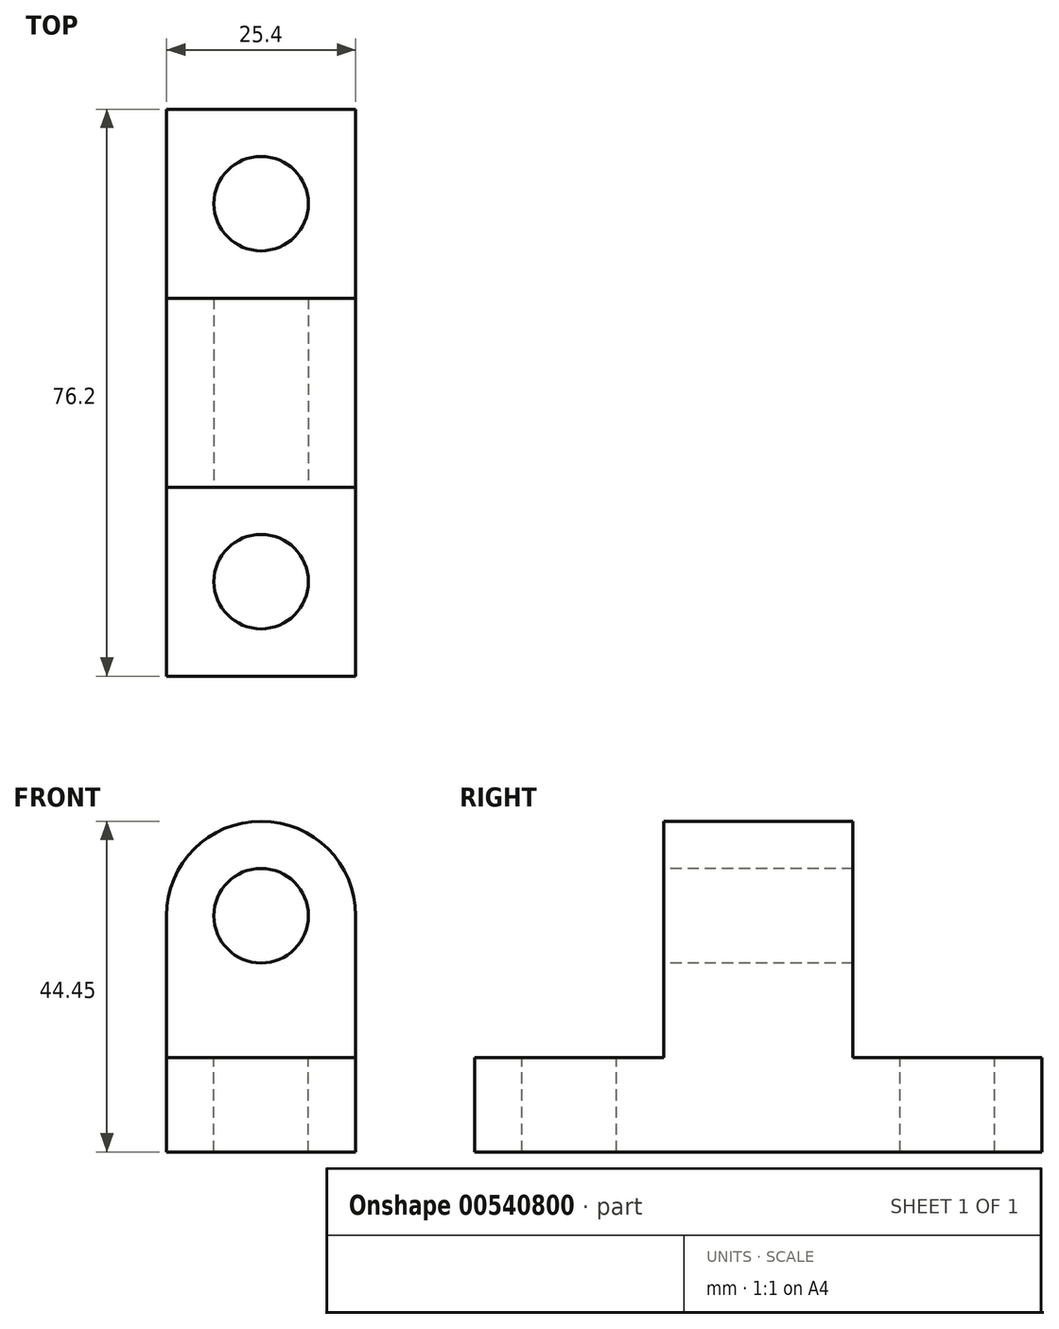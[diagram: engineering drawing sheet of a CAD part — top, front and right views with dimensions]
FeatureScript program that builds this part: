
annotation { "Feature Type Name" : "Feature", "Feature Type Description" : "" }
export const myFeature = defineFeature(function(context is Context, id is Id, definition is map)
    precondition{}
    {
        {
            var Q0;
            Q0=qCreatedBy(makeId("Top.planeOp"),FACE);
            var sketch = newSketch(context, id + "F0", { "sketchPlane" : qUnion([Q0])});
            skLineSegment(sketch, "E0", {"start": v(0, 0) * mm, "end": v(0, 76.2) * mm});
            skLineSegment(sketch, "E1", {"start": v(0, 76.2) * mm, "end": v(25.4, 76.2) * mm});
            skLineSegment(sketch, "E2", {"start": v(25.4, 76.2) * mm, "end": v(25.4, 0) * mm});
            skLineSegment(sketch, "E3", {"start": v(25.4, 0) * mm, "end": v(0, 0) * mm});
            skSolve(sketch);
        }
        {
            var Q0;
            Q0=makeQuery(id+"F0.imprint","IMPRINT",FACE,{"disambiguationData":[TD([[makeQuery(id+"F0.imprint","IMPRINT",EDGE,{"derivedFrom":sQuery(id+"F0.wireOp",EDGE,"E0")}),-1.0]])]});
            extrude(context, id + "F1", {"entities" : qUnion([Q0]), "depth" : 44.45 * mm, "offsetDistance" : 25.4 * mm});
        }
        {
            var Q0;
            Q0=makeQuery(id+"F1.opExtrude","SWEPT_FACE",FACE,{"disambiguationData":[OSD([sQuery(id+"F0.wireOp",EDGE,"E0")])]});
            var sketch = newSketch(context, id + "F2", { "sketchPlane" : qUnion([Q0])});
            skLineSegment(sketch, "E4", {"start": v(0, 12.7) * mm, "end": v(-25.4, 12.7) * mm});
            skLineSegment(sketch, "E5", {"start": v(-25.4, 12.7) * mm, "end": v(-25.4, 44.45) * mm});
            skLineSegment(sketch, "E6", {"start": v(-25.4, 44.45) * mm, "end": v(0, 44.45) * mm});
            skLineSegment(sketch, "E7", {"start": v(0, 44.45) * mm, "end": v(0, 12.7) * mm});
            skLineSegment(sketch, "E8", {"start": v(-76.2, 12.7) * mm, "end": v(-50.8, 12.7) * mm});
            skLineSegment(sketch, "E9", {"start": v(-50.8, 12.7) * mm, "end": v(-50.8, 44.45) * mm});
            skLineSegment(sketch, "E10", {"start": v(-50.8, 44.45) * mm, "end": v(-76.2, 44.45) * mm});
            skLineSegment(sketch, "E11", {"start": v(-76.2, 44.45) * mm, "end": v(-76.2, 12.7) * mm});
            skSolve(sketch);
        }
        {
            var Q0;
            Q0=makeQuery(id+"F2.imprint","IMPRINT",FACE,{"disambiguationData":[TD([[makeQuery(id+"F2.imprint","IMPRINT",EDGE,{"derivedFrom":sQuery(id+"F2.wireOp",EDGE,"E8")}),1.0]])]});
            var Q1;
            Q1=makeQuery(id+"F2.imprint","IMPRINT",FACE,{"disambiguationData":[TD([[makeQuery(id+"F2.imprint","IMPRINT",EDGE,{"derivedFrom":sQuery(id+"F2.wireOp",EDGE,"E4")}),-1.0]])]});
            extrude(context, id + "F3", {"entities" : qUnion([Q0, Q1]), "operationType" : NewBodyOperationType.REMOVE, "oppositeDirection" : true, "depth" : 25.4 * mm, "offsetDistance" : 25.4 * mm});
        }
        {
            var Q0;
            Q0=makeQuery(id+"F3.boolean.opBoolean","COPY",FACE,{"derivedFrom":makeQuery(id+"F3.opExtrude","SWEPT_FACE",FACE,{"disambiguationData":[OSD([sQuery(id+"F2.wireOp",EDGE,"E5")])]})});
            var sketch = newSketch(context, id + "F4", { "sketchPlane" : qUnion([Q0])});
            skLineSegment(sketch, "E12", {"start": v(25.4, 24.96) * mm, "end": v(25.4, 44.45) * mm});
            skLineSegment(sketch, "E13", {"start": v(25.4, 44.45) * mm, "end": v(0, 44.45) * mm});
            skLineSegment(sketch, "E14", {"start": v(0, 44.45) * mm, "end": v(0, 28.57) * mm});
            skArc(sketch, "E15", {"start": v(25.4, 31.75) * mm, "mid": v(12.7, 44.45) * mm, "end": v(0, 31.75) * mm});
            skSolve(sketch);
        }
        {
            var Q0;
            {var subQ0=sQuery(id+"F4.wireOp",EDGE,"E14");var subQ1=sQuery(id+"F4.wireOp",EDGE,"E13");var subQ2=makeQuery(id+"F4.imprint","INTERSECT",VERTEX,{"derivedFrom":[subQ1,subQ0]});Q0=makeQuery(id+"F4.imprint","IMPRINT",FACE,{"disambiguationData":[TD([[makeQuery(id+"F4.imprint","IMPRINT",EDGE,{"disambiguationData":[TD([[subQ2,1.0]])],"derivedFrom":subQ1}),1.0]])]});}
            var Q1;
            {var subQ0=sQuery(id+"F4.wireOp",EDGE,"E13");var subQ1=sQuery(id+"F4.wireOp",EDGE,"E12");var subQ2=makeQuery(id+"F4.imprint","INTERSECT",VERTEX,{"derivedFrom":[subQ1,subQ0]});Q1=makeQuery(id+"F4.imprint","IMPRINT",FACE,{"disambiguationData":[TD([[makeQuery(id+"F4.imprint","IMPRINT",EDGE,{"disambiguationData":[TD([[subQ2,1.0]])],"derivedFrom":subQ1}),1.0]])]});}
            extrude(context, id + "F5", {"entities" : qUnion([Q0, Q1]), "operationType" : NewBodyOperationType.REMOVE, "oppositeDirection" : true, "depth" : 25.4 * mm, "offsetDistance" : 25.4 * mm});
        }
        {
            var Q0;
            Q0=makeQuery(id+"F3.boolean.opBoolean","COPY",FACE,{"derivedFrom":makeQuery(id+"F3.opExtrude","SWEPT_FACE",FACE,{"disambiguationData":[OSD([sQuery(id+"F2.wireOp",EDGE,"E5")])]})});
            var sketch = newSketch(context, id + "F6", { "sketchPlane" : qUnion([Q0])});
            skLineSegment(sketch, "E16", {"start": v(25.4, 12.7) * mm, "end": v(25.4, 31.75) * mm});
            skLineSegment(sketch, "E17", {"start": v(0, 31.75) * mm, "end": v(0, 12.7) * mm});
            skLineSegment(sketch, "E18", {"start": v(0, 12.7) * mm, "end": v(25.4, 12.7) * mm});
            skEllipse(sketch, "E19", {"center": v(12.7, 31.75) * mm, "majorRadius": 6.35 * mm, "minorRadius": 6.35 * mm, "majorAxis": v(1, 0)});
            skSolve(sketch);
        }
        {
            var Q0;
            Q0=makeQuery(id+"F6.imprint","IMPRINT",FACE,{"disambiguationData":[TD([[makeQuery(id+"F6.imprint","IMPRINT",EDGE,{"derivedFrom":sQuery(id+"F6.wireOp",EDGE,"E19")}),1.0]])]});
            extrude(context, id + "F7", {"entities" : qUnion([Q0]), "operationType" : NewBodyOperationType.REMOVE, "oppositeDirection" : true, "depth" : 25.4 * mm, "offsetDistance" : 25.4 * mm});
        }
        {
            var Q0;
            Q0=makeQuery(id+"F3.boolean.opBoolean","COPY",FACE,{"derivedFrom":makeQuery(id+"F3.opExtrude","SWEPT_FACE",FACE,{"disambiguationData":[OSD([sQuery(id+"F2.wireOp",EDGE,"E4")])]})});
            var sketch = newSketch(context, id + "F8", { "sketchPlane" : qUnion([Q0])});
            skCircle(sketch, "E20", {"center": v(12.7, 12.7) * mm, "radius": 6.35 * mm});
            skSolve(sketch);
        }
        {
            var Q0;
            Q0 = qSketchRegion(id + "F8", true);
            extrude(context, id + "F9", {"entities" : qUnion([Q0]), "operationType" : NewBodyOperationType.REMOVE, "oppositeDirection" : true, "depth" : 25.4 * mm, "offsetDistance" : 25.4 * mm});
        }
        {
            var Q0;
            Q0=makeQuery(id+"F3.boolean.opBoolean","COPY",FACE,{"derivedFrom":makeQuery(id+"F3.opExtrude","SWEPT_FACE",FACE,{"disambiguationData":[OSD([sQuery(id+"F2.wireOp",EDGE,"E8")])]})});
            var sketch = newSketch(context, id + "F10", { "sketchPlane" : qUnion([Q0])});
            skCircle(sketch, "E21", {"center": v(12.7, 63.5) * mm, "radius": 6.35 * mm});
            skPoint(sketch, "E21.centerSnap0", {"position": v(12.7, 76.2) * mm});
            skSolve(sketch);
        }
        {
            var Q0;
            Q0=makeQuery(id+"F10.imprint","IMPRINT",FACE,{"disambiguationData":[TD([[makeQuery(id+"F10.imprint","IMPRINT",EDGE,{"derivedFrom":sQuery(id+"F10.wireOp",EDGE,"E21")}),1.0]])]});
            extrude(context, id + "F11", {"entities" : qUnion([Q0]), "operationType" : NewBodyOperationType.REMOVE, "oppositeDirection" : true, "depth" : 25.4 * mm, "offsetDistance" : 25.4 * mm});
        }
    });
